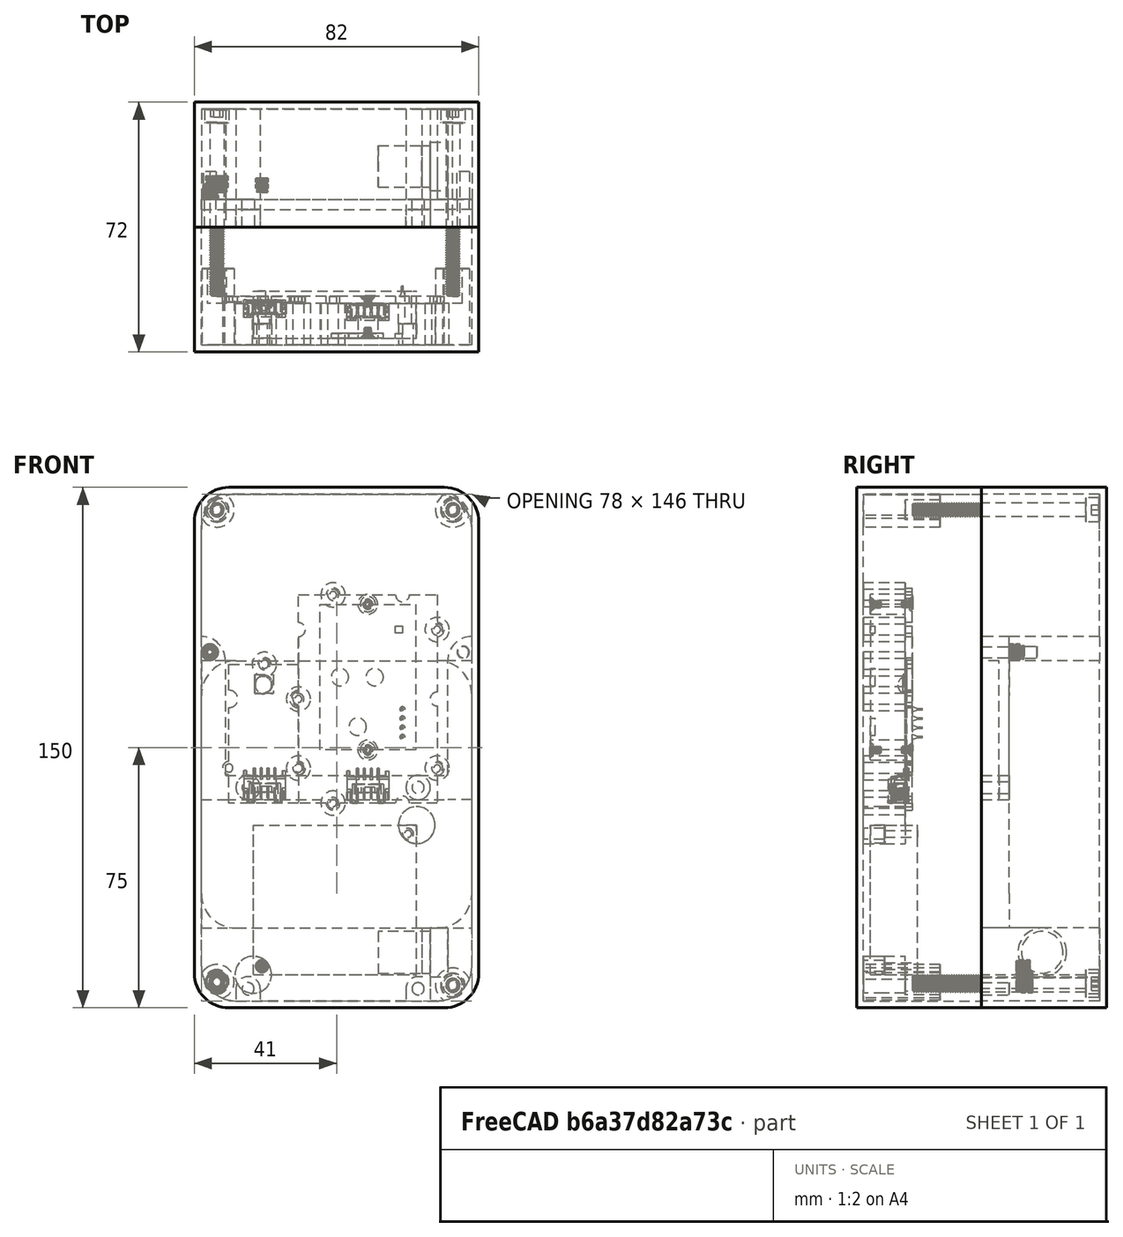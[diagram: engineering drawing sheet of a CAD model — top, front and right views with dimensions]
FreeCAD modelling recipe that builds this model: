
FCSTD DOCUMENT  (FreeCAD 0.20R29177 +233 (Git))
Label: wearableCad_10_10_2022
License: All rights reserved
LicenseURL: http://en.wikipedia.org/wiki/All_rights_reserved
objects: Part::Cylinder×78, Part::Cut×42, Part::Box×36, Part::MultiFuse×24, Part::Feature×10
note: 190 computed .brp shape members not serialized (recipe doc carries the construction recipe); baked Part::Feature solids carry a one-line shape summary decoded from their .brp

FEATURE [Part::Feature] Feature  label="Odroid-C4"
  Placement = pos=(66,-10,0) rot=(0.57735,-0.57735,0.57735;2.0944rad)
  shape: bbox 57.1 x 20.65 x 89.5 mm, 2775 faces, 0 solids (baked)
FEATURE [Part::Feature] Feature001  label="SCD30"
  Placement = pos=(-1.3e-14,-22,57) rot=(0,-1,0;1.5708rad)
  shape: bbox 44 x 15.1 x 64 mm, 422 faces, 13 solids (baked)
FEATURE [Part::Feature] Feature002  label="bme280"
  Placement = pos=(-60,-20,58) rot=(0.707107,0,0.707107;3.14159rad)
  shape: bbox 23.8 x 6.016 x 41.9 mm, 221 faces, 2 solids (baked)
FEATURE [Part::MultiFuse] Fusion  label="i2cSensors"
  Placement = pos=(68,-10,0) rot=(0,0,1;0rad)
  Shapes = -> [Feature001,Feature002]
FEATURE [Part::Box] Box  label="ips7100"
  AttacherType = Attacher::AttachEngine3D
  Height = 43.1
  Length = 47.1
  Width = 13.55
FEATURE [Part::Cylinder] Cylinder
  Angle = 360
  AttacherType = Attacher::AttachEngine3D
  FirstAngle = 0
  Height = 13.55
  Placement = pos=(2.5,13.55,2.5) rot=(1,0,0;1.5708rad)
  Radius = 1
  SecondAngle = 0
FEATURE [Part::Cylinder] Cylinder001  label="semiCut"
  Angle = 90
  AttacherType = Attacher::AttachEngine3D
  FirstAngle = 0
  Height = 4.13
  Placement = pos=(0,4.13,-9e-16) rot=(1,0,0;1.5708rad)
  Radius = 5.25
  SecondAngle = 0
FEATURE [Part::MultiFuse] Fusion001  label="ipsCut"
  Shapes = -> [Cylinder,Cylinder001]
FEATURE [Part::Cylinder] Cylinder002
  Angle = 360
  AttacherType = Attacher::AttachEngine3D
  FirstAngle = 0
  Height = 13.55
  Placement = pos=(2.5,13.55,2.5) rot=(1,0,0;1.5708rad)
  Radius = 1
  SecondAngle = 0
FEATURE [Part::Cylinder] Cylinder003  label="semiCut001"
  Angle = 90
  AttacherType = Attacher::AttachEngine3D
  FirstAngle = 0
  Height = 4.13
  Placement = pos=(0,4.13,-9e-16) rot=(1,0,0;1.5708rad)
  Radius = 5.25
  SecondAngle = 0
FEATURE [Part::MultiFuse] Fusion002  label="ipsCut001"
  Placement = pos=(47.1,0,43.1) rot=(0,1,0;3.14159rad)
  Shapes = -> [Cylinder002,Cylinder003]
FEATURE [Part::MultiFuse] Fusion003
  Shapes = -> [Fusion001,Fusion002]
FEATURE [Part::Cut] Cut  label="ips7100V"
  Base = -> Box
  Placement = pos=(15,-42,7.55) rot=(0,0,1;0rad)
  Tool = -> Fusion003
FEATURE [Part::Box] Box001  label="V25B"
  AttacherType = Attacher::AttachEngine3D
  Height = 77
  Length = 78
  Width = 26
FEATURE [Part::Cylinder] Cylinder004
  Angle = 90
  AttacherType = Attacher::AttachEngine3D
  FirstAngle = 0
  Height = 26
  Placement = pos=(0,26,-5.8e-15) rot=(1,0,0;1.5708rad)
  Radius = 10
  SecondAngle = 0
FEATURE [Part::Box] Box002  label="Cube"
  AttacherType = Attacher::AttachEngine3D
  Height = 10
  Length = 10
  Width = 26
FEATURE [Part::Cut] Cut001
  Base = -> Box002
  Placement = pos=(68,0,67) rot=(0,0,1;0rad)
  Tool = -> Cylinder004
FEATURE [Part::Box] Box003  label="Cube001"
  AttacherType = Attacher::AttachEngine3D
  Height = 10
  Length = 10
  Width = 26
FEATURE [Part::Cylinder] Cylinder005
  Angle = 90
  AttacherType = Attacher::AttachEngine3D
  FirstAngle = 0
  Height = 26
  Placement = pos=(0,26,-5.8e-15) rot=(1,0,0;1.5708rad)
  Radius = 10
  SecondAngle = 0
FEATURE [Part::Cut] Cut002
  Base = -> Box003
  Placement = pos=(68,0,10) rot=(0,1,0;1.5708rad)
  Tool = -> Cylinder005
FEATURE [Part::Box] Box004  label="Cube002"
  AttacherType = Attacher::AttachEngine3D
  Height = 10
  Length = 10
  Width = 26
FEATURE [Part::Cylinder] Cylinder006
  Angle = 90
  AttacherType = Attacher::AttachEngine3D
  FirstAngle = 0
  Height = 26
  Placement = pos=(0,26,-5.8e-15) rot=(1,0,0;1.5708rad)
  Radius = 10
  SecondAngle = 0
FEATURE [Part::Cut] Cut003
  Base = -> Box004
  Placement = pos=(10,0,10) rot=(0,1,0;3.14159rad)
  Tool = -> Cylinder006
FEATURE [Part::Box] Box005  label="Cube003"
  AttacherType = Attacher::AttachEngine3D
  Height = 10
  Length = 10
  Width = 26
FEATURE [Part::Cylinder] Cylinder007
  Angle = 90
  AttacherType = Attacher::AttachEngine3D
  FirstAngle = 0
  Height = 26
  Placement = pos=(0,26,-5.8e-15) rot=(1,0,0;1.5708rad)
  Radius = 10
  SecondAngle = 0
FEATURE [Part::Cut] Cut004
  Base = -> Box005
  Placement = pos=(10,0,67) rot=(0,-1,0;1.5708rad)
  Tool = -> Cylinder007
FEATURE [Part::MultiFuse] Fusion004  label="v25Cuts"
  Shapes = -> [Cut001,Cut002,Cut003,Cut004]
FEATURE [Part::Cut] Cut005  label="V25B001"
  Base = -> Box001
  Placement = pos=(0,-2,21) rot=(0,0,1;0rad)
  Tool = -> Fusion004
FEATURE [Part::Box] Box007  label="Cube004"
  AttacherType = Attacher::AttachEngine3D
  Height = 10
  Length = 10
  Placement = pos=(0,-10,0) rot=(0,0,1;0rad)
  Width = 36
FEATURE [Part::Cylinder] Cylinder008
  Angle = 90
  AttacherType = Attacher::AttachEngine3D
  FirstAngle = 0
  Height = 36
  Placement = pos=(0,26,-5.8e-15) rot=(1,0,0;1.5708rad)
  Radius = 10
  SecondAngle = 0
FEATURE [Part::Cut] Cut006
  Base = -> Box007
  Placement = pos=(8,18,8) rot=(-0.707107,0,0.707107;3.14159rad)
  Tool = -> Cylinder008
FEATURE [Part::Box] Box008  label="baseOut001"
  AttacherType = Attacher::AttachEngine3D
  Height = 150
  Length = 82
  Placement = pos=(80,26,-2) rot=(0,0,1;3.14159rad)
  Width = 36
FEATURE [Part::Box] Box009  label="Cube005"
  AttacherType = Attacher::AttachEngine3D
  Height = 10
  Length = 10
  Placement = pos=(0,-10,0) rot=(0,0,1;0rad)
  Width = 36
FEATURE [Part::Cylinder] Cylinder009
  Angle = 90
  AttacherType = Attacher::AttachEngine3D
  FirstAngle = 0
  Height = 36
  Placement = pos=(0,26,-5.8e-15) rot=(1,0,0;1.5708rad)
  Radius = 10
  SecondAngle = 0
FEATURE [Part::Cut] Cut007
  Base = -> Box009
  Placement = pos=(70,18,8) rot=(1,0,0;3.14159rad)
  Tool = -> Cylinder009
FEATURE [Part::Box] Box010  label="Cube006"
  AttacherType = Attacher::AttachEngine3D
  Height = 10
  Length = 10
  Placement = pos=(0,-10,0) rot=(0,0,1;0rad)
  Width = 36
FEATURE [Part::Cylinder] Cylinder010
  Angle = 90
  AttacherType = Attacher::AttachEngine3D
  FirstAngle = 0
  Height = 36
  Placement = pos=(0,26,-5.8e-15) rot=(1,0,0;1.5708rad)
  Radius = 10
  SecondAngle = 0
FEATURE [Part::Cut] Cut008
  Base = -> Box010
  Placement = pos=(8,18,138) rot=(0,0,1;3.14159rad)
  Tool = -> Cylinder010
FEATURE [Part::Box] Box011  label="Cube007"
  AttacherType = Attacher::AttachEngine3D
  Height = 10
  Length = 10
  Placement = pos=(0,-10,0) rot=(0,0,1;0rad)
  Width = 36
FEATURE [Part::Cylinder] Cylinder011
  Angle = 90
  AttacherType = Attacher::AttachEngine3D
  FirstAngle = 0
  Height = 36
  Placement = pos=(0,26,-5.8e-15) rot=(1,0,0;1.5708rad)
  Radius = 10
  SecondAngle = 0
FEATURE [Part::Cut] Cut009
  Base = -> Box011
  Placement = pos=(70,18,138) rot=(0.707107,0,0.707107;3.14159rad)
  Tool = -> Cylinder011
FEATURE [Part::MultiFuse] Fusion005
  Placement = pos=(0,-2,0) rot=(0,0,1;0rad)
  Shapes = -> [Cut006,Cut007,Cut008,Cut009]
FEATURE [Part::Cut] Cut010  label="BaseOut"
  Base = -> Box008
  Tool = -> Fusion005
FEATURE [Part::Box] Box013  label="Cube009"
  AttacherType = Attacher::AttachEngine3D
  Height = 10
  Length = 10
  Placement = pos=(0,-8,0) rot=(0,0,1;0rad)
  Width = 34
FEATURE [Part::Box] Box014  label="baseOut002"
  AttacherType = Attacher::AttachEngine3D
  Height = 146
  Length = 78
  Placement = pos=(80,26,-2) rot=(0,0,1;3.14159rad)
  Width = 34
FEATURE [Part::Box] Box015  label="Cube010"
  AttacherType = Attacher::AttachEngine3D
  Height = 10
  Length = 10
  Placement = pos=(0,-8,0) rot=(0,0,1;0rad)
  Width = 34
FEATURE [Part::Box] Box016  label="Cube011"
  AttacherType = Attacher::AttachEngine3D
  Height = 10
  Length = 10
  Placement = pos=(0,-8,0) rot=(0,0,1;0rad)
  Width = 34
FEATURE [Part::Box] Box017  label="Cube012"
  AttacherType = Attacher::AttachEngine3D
  Height = 10
  Length = 10
  Placement = pos=(0,-8,0) rot=(0,0,1;0rad)
  Width = 34
FEATURE [Part::Cylinder] Cylinder013
  Angle = 90
  AttacherType = Attacher::AttachEngine3D
  FirstAngle = 0
  Height = 34
  Placement = pos=(0,26,-5.8e-15) rot=(1,0,0;1.5708rad)
  Radius = 10
  SecondAngle = 0
FEATURE [Part::Cut] Cut012
  Base = -> Box013
  Placement = pos=(12,18,8) rot=(0.707107,0,-0.707107;3.14159rad)
  Tool = -> Cylinder013
FEATURE [Part::Cylinder] Cylinder014
  Angle = 90
  AttacherType = Attacher::AttachEngine3D
  FirstAngle = 0
  Height = 34
  Placement = pos=(0,26,-5.8e-15) rot=(1,0,0;1.5708rad)
  Radius = 10
  SecondAngle = 0
FEATURE [Part::Cut] Cut013
  Base = -> Box015
  Placement = pos=(70,18,8) rot=(1,0,0;3.14159rad)
  Tool = -> Cylinder014
FEATURE [Part::Cylinder] Cylinder015
  Angle = 90
  AttacherType = Attacher::AttachEngine3D
  FirstAngle = 0
  Height = 34
  Placement = pos=(0,26,-5.8e-15) rot=(1,0,0;1.5708rad)
  Radius = 10
  SecondAngle = 0
FEATURE [Part::Cut] Cut014
  Base = -> Box016
  Placement = pos=(12,18,134) rot=(0,0,1;3.14159rad)
  Tool = -> Cylinder015
FEATURE [Part::Cylinder] Cylinder016
  Angle = 90
  AttacherType = Attacher::AttachEngine3D
  FirstAngle = 0
  Height = 34
  Placement = pos=(0,26,-5.8e-15) rot=(1,0,0;1.5708rad)
  Radius = 10
  SecondAngle = 0
FEATURE [Part::Cut] Cut015
  Base = -> Box017
  Placement = pos=(70,18,135) rot=(0.707107,0,0.707107;3.14159rad)
  Tool = -> Cylinder016
FEATURE [Part::MultiFuse] Fusion006
  Shapes = -> [Cut012,Cut013,Cut014,Cut015]
FEATURE [Part::Cut] Cut016  label="BaseOut001"
  Base = -> Box014
  Placement = pos=(-2,-2,2) rot=(0,0,1;0rad)
  Tool = -> Fusion006
FEATURE [Part::Cut] Cut017  label="baseOut"
  Base = -> Cut010
  Tool = -> Cut016
FEATURE [Part::Box] Box018  label="Cube013"
  AttacherType = Attacher::AttachEngine3D
  Height = 10
  Length = 10
  Placement = pos=(10,26,0) rot=(0,0,-1;3.14159rad)
  Width = 26
FEATURE [Part::Cylinder] Cylinder017
  Angle = 90
  AttacherType = Attacher::AttachEngine3D
  FirstAngle = 0
  Height = 26
  Placement = pos=(0,26,-5.8e-15) rot=(1,0,0;1.5708rad)
  Radius = 10
  SecondAngle = 0
FEATURE [Part::Cut] Cut018  label="batterySupport"
  Base = -> Box018
  Placement = pos=(10,-2,31) rot=(0,1,0;3.14159rad)
  Tool = -> Cylinder017
FEATURE [Part::Box] Box019  label="Cube014"
  AttacherType = Attacher::AttachEngine3D
  Height = 10
  Length = 10
  Placement = pos=(10,26,0) rot=(0,0,1;3.14159rad)
  Width = 26
FEATURE [Part::Cylinder] Cylinder018
  Angle = 90
  AttacherType = Attacher::AttachEngine3D
  FirstAngle = 0
  Height = 26
  Placement = pos=(0,26,-5.8e-15) rot=(1,0,0;1.5708rad)
  Radius = 10
  SecondAngle = 0
FEATURE [Part::Cut] Cut019  label="batterySupport001"
  Base = -> Box019
  Placement = pos=(68,-2,31) rot=(0,-1,0;4.71239rad)
  Tool = -> Cylinder018
FEATURE [Part::Box] Box020  label="Cube015"
  AttacherType = Attacher::AttachEngine3D
  Height = 10
  Length = 10
  Placement = pos=(10,26,0) rot=(0,0,1;3.14159rad)
  Width = 26
FEATURE [Part::Cylinder] Cylinder019
  Angle = 90
  AttacherType = Attacher::AttachEngine3D
  FirstAngle = 0
  Height = 26
  Placement = pos=(0,26,-5.8e-15) rot=(1,0,0;1.5708rad)
  Radius = 10
  SecondAngle = 0
FEATURE [Part::Cut] Cut020  label="batterySupport002"
  Base = -> Box020
  Placement = pos=(68,-2,88) rot=(0,0,1;0rad)
  Tool = -> Cylinder019
FEATURE [Part::Box] Box021  label="Cube016"
  AttacherType = Attacher::AttachEngine3D
  Height = 10
  Length = 10
  Placement = pos=(10,26,0) rot=(0,0,1;3.14159rad)
  Width = 26
FEATURE [Part::Cylinder] Cylinder020
  Angle = 90
  AttacherType = Attacher::AttachEngine3D
  FirstAngle = 0
  Height = 26
  Placement = pos=(0,26,-5.8e-15) rot=(1,0,0;1.5708rad)
  Radius = 10
  SecondAngle = 0
FEATURE [Part::Cut] Cut021  label="batterySupport003"
  Base = -> Box021
  Placement = pos=(10,-2,88) rot=(0,1,0;4.71239rad)
  Tool = -> Cylinder020
FEATURE [Part::Cylinder] Cylinder021
  Angle = 360
  AttacherType = Attacher::AttachEngine3D
  FirstAngle = 0
  Height = 34
  Placement = pos=(13.5,24,3.5) rot=(1,0,0;1.5708rad)
  Radius = 3.5
  SecondAngle = 0
FEATURE [Part::Cylinder] Cylinder022
  Angle = 360
  AttacherType = Attacher::AttachEngine3D
  FirstAngle = 0
  Height = 8
  Placement = pos=(13.5,-2,3.5) rot=(1,0,0;1.5708rad)
  Radius = 1.75
  SecondAngle = 0
FEATURE [Part::Box] Box022  label="Cube017"
  AttacherType = Attacher::AttachEngine3D
  Height = 3.5
  Length = 7
  Placement = pos=(10,24,3.5) rot=(1,0,0;3.14159rad)
  Width = 34
FEATURE [Part::Cylinder] Cylinder023
  Angle = 360
  AttacherType = Attacher::AttachEngine3D
  FirstAngle = 0
  Height = 34
  Placement = pos=(62.5,24,3.5) rot=(1,0,0;1.5708rad)
  Radius = 3.5
  SecondAngle = 0
FEATURE [Part::Cylinder] Cylinder024
  Angle = 360
  AttacherType = Attacher::AttachEngine3D
  FirstAngle = 0
  Height = 8
  Placement = pos=(62.5,-2,3.5) rot=(1,0,0;1.5708rad)
  Radius = 1.75
  SecondAngle = 0
FEATURE [Part::Box] Box023  label="Cube018"
  AttacherType = Attacher::AttachEngine3D
  Height = 3.5
  Length = 7
  Placement = pos=(59,24,3.5) rot=(1,0,0;3.14159rad)
  Width = 34
FEATURE [Part::Cylinder] Cylinder025
  Angle = 360
  AttacherType = Attacher::AttachEngine3D
  FirstAngle = 0
  Height = 20
  Radius = 6
  SecondAngle = 0
FEATURE [Part::Cylinder] Cylinder026
  Angle = 360
  AttacherType = Attacher::AttachEngine3D
  FirstAngle = 0
  Height = 5
  Radius = 7
  SecondAngle = 0
FEATURE [Part::MultiFuse] Fusion007  label="powerSwitch"
  Placement = pos=(71,7.5,14) rot=(0,1,0;4.71239rad)
  Shapes = -> [Cylinder025,Cylinder026]
FEATURE [Part::Box] Box024  label="Cube019"
  AttacherType = Attacher::AttachEngine3D
  Height = 17.5
  Length = 2.5
  Placement = pos=(63.5,24,21) rot=(1,0,0;3.14159rad)
  Width = 34
FEATURE [Part::MultiFuse] Fusion008  label="base"
  Shapes = -> [Cut017,Cut018,Cut019,Cut020,Cut021]
FEATURE [Part::MultiFuse] Fusion009  label="base001"
  Shapes = -> [Cylinder021,Cylinder023,Box022,Box023,Box024,Fusion008]
FEATURE [Part::MultiFuse] Fusion010  label="baseCuts"
  Shapes = -> [Cylinder024,Cylinder022,Fusion007]
FEATURE [Part::Cut] Cut022  label="base002"
  Base = -> Fusion009
  Tool = -> Fusion010
FEATURE [Part::Cylinder] Cylinder027  label="mainMounts"
  Angle = 90
  AttacherType = Attacher::AttachEngine3D
  FirstAngle = 0
  Height = 26
  Placement = pos=(0,24,98) rot=(1,0,0;1.5708rad)
  Radius = 7
  SecondAngle = 0
FEATURE [Part::Cylinder] Cylinder028  label="mainMounts001"
  Angle = 90
  AttacherType = Attacher::AttachEngine3D
  FirstAngle = 0
  Height = 26
  Placement = pos=(78,24,98) rot=(0.57735,-0.57735,0.57735;2.0944rad)
  Radius = 7
  SecondAngle = 0
FEATURE [Part::Cylinder] Cylinder029
  Angle = 360
  AttacherType = Attacher::AttachEngine3D
  FirstAngle = 0
  Height = 8
  Placement = pos=(2.5,-2,100.5) rot=(1,0,0;1.5708rad)
  Radius = 1.75
  SecondAngle = 0
FEATURE [Part::Cylinder] Cylinder030
  Angle = 360
  AttacherType = Attacher::AttachEngine3D
  FirstAngle = 0
  Height = 8
  Placement = pos=(75.5,-2,100.5) rot=(1,0,0;1.5708rad)
  Radius = 1.75
  SecondAngle = 0
FEATURE [Part::MultiFuse] Fusion011  label="baseCuts001"
  Placement = pos=(0,8,0) rot=(0,0,1;0rad)
  Shapes = -> [Cylinder029,Cylinder030]
FEATURE [Part::MultiFuse] Fusion012
  Shapes = -> [Cylinder028,Cylinder027]
FEATURE [Part::MultiFuse] Fusion013  label="base003"
  Shapes = -> [Cut022,Fusion012]
FEATURE [Part::Cut] Cut023  label="baseBottom"
  Base = -> Fusion013
  Tool = -> Fusion011
FEATURE [Part::Feature] Solid  label="m3HeatSet"
  Placement = pos=(2.5,2.3,100.5) rot=(1,0,0;3.14159rad)
  shape: bbox 4.772 x 4.354 x 4.772 mm, 239 faces (baked)
FEATURE [Part::Cylinder] Cylinder031
  Angle = 360
  AttacherType = Attacher::AttachEngine3D
  FirstAngle = 0
  Height = 8
  Placement = pos=(13.5,-2,61.5) rot=(1,0,0;1.5708rad)
  Radius = 3.5
  SecondAngle = 0
FEATURE [Part::Cylinder] Cylinder032  label="cuts"
  Angle = 360
  AttacherType = Attacher::AttachEngine3D
  FirstAngle = 0
  Height = 8
  Placement = pos=(13.5,-2,61.5) rot=(1,0,0;1.5708rad)
  Radius = 1.75
  SecondAngle = 0
FEATURE [Part::Cylinder] Cylinder034
  Angle = 360
  AttacherType = Attacher::AttachEngine3D
  FirstAngle = 0
  Height = 8
  Placement = pos=(62.5,-2,61.5) rot=(1,0,0;1.5708rad)
  Radius = 3.5
  SecondAngle = 0
FEATURE [Part::Cylinder] Cylinder035  label="cuts001"
  Angle = 360
  AttacherType = Attacher::AttachEngine3D
  FirstAngle = 0
  Height = 8
  Placement = pos=(62.5,-2,61.5) rot=(1,0,0;1.5708rad)
  Radius = 1.75
  SecondAngle = 0
FEATURE [Part::Cylinder] Cylinder036
  Angle = 90
  AttacherType = Attacher::AttachEngine3D
  FirstAngle = 0
  Height = 8
  Placement = pos=(78,-2,98) rot=(-0.57735,0.57735,-0.57735;4.18879rad)
  Radius = 7
  SecondAngle = 0
FEATURE [Part::Cylinder] Cylinder037
  Angle = 90
  AttacherType = Attacher::AttachEngine3D
  FirstAngle = 0
  Height = 8
  Placement = pos=(0,-2,98) rot=(1,0,0;1.5708rad)
  Radius = 7
  SecondAngle = 0
FEATURE [Part::Box] Box025  label="Cube020"
  AttacherType = Attacher::AttachEngine3D
  Height = 7
  Length = 78
  Placement = pos=(0,-5,58) rot=(0,0,1;0rad)
  Width = 3
FEATURE [Part::Box] Box026  label="Cube021"
  AttacherType = Attacher::AttachEngine3D
  Height = 7
  Length = 40
  Placement = pos=(7,-5,58) rot=(0,1,0;4.71239rad)
  Width = 3
FEATURE [Part::Box] Box027  label="Cube022"
  AttacherType = Attacher::AttachEngine3D
  Height = 7
  Length = 40
  Placement = pos=(78,-5,58) rot=(0,-1,0;1.5708rad)
  Width = 3
FEATURE [Part::MultiFuse] Fusion014
  Shapes = -> [Box027,Box025,Box026,Cylinder034,Cylinder031]
FEATURE [Part::Cylinder] Cylinder038  label="m3Screw"
  Angle = 360
  AttacherType = Attacher::AttachEngine3D
  FirstAngle = 0
  Height = 8
  Placement = pos=(75.5,-2,100.5) rot=(1,0,0;1.5708rad)
  Radius = 1.6
  SecondAngle = 0
FEATURE [Part::Cylinder] Cylinder039  label="m3Screw001"
  Angle = 360
  AttacherType = Attacher::AttachEngine3D
  FirstAngle = 0
  Height = 8
  Placement = pos=(2.5,-2,100.5) rot=(1,0,0;1.5708rad)
  Radius = 1.6
  SecondAngle = 0
FEATURE [Part::MultiFuse] Fusion015  label="c4Hold"
  Shapes = -> [Cylinder036,Cylinder037,Fusion014]
FEATURE [Part::MultiFuse] Fusion016  label="c4oldCuts"
  Shapes = -> [Cylinder039,Cylinder032,Cylinder035,Cylinder038]
FEATURE [Part::Cut] Cut024  label="c4Hold001"
  Base = -> Fusion015
  Tool = -> Fusion016
FEATURE [Part::Box] Box028  label="Cube023"
  AttacherType = Attacher::AttachEngine3D
  Height = 10
  Length = 10
  Placement = pos=(0,-10,0) rot=(0,0,1;0rad)
  Width = 36
FEATURE [Part::Box] Box029  label="baseOut003"
  AttacherType = Attacher::AttachEngine3D
  Height = 150
  Length = 82
  Placement = pos=(80,26,-2) rot=(0,0,1;3.14159rad)
  Width = 36
FEATURE [Part::Box] Box030  label="Cube024"
  AttacherType = Attacher::AttachEngine3D
  Height = 10
  Length = 10
  Placement = pos=(0,-10,0) rot=(0,0,1;0rad)
  Width = 36
FEATURE [Part::Box] Box031  label="Cube025"
  AttacherType = Attacher::AttachEngine3D
  Height = 10
  Length = 10
  Placement = pos=(0,-10,0) rot=(0,0,1;0rad)
  Width = 36
FEATURE [Part::Box] Box032  label="Cube026"
  AttacherType = Attacher::AttachEngine3D
  Height = 10
  Length = 10
  Placement = pos=(0,-10,0) rot=(0,0,1;0rad)
  Width = 36
FEATURE [Part::Box] Box033  label="Cube027"
  AttacherType = Attacher::AttachEngine3D
  Height = 10
  Length = 10
  Placement = pos=(0,-8,0) rot=(0,0,1;0rad)
  Width = 34
FEATURE [Part::Box] Box034  label="baseOut004"
  AttacherType = Attacher::AttachEngine3D
  Height = 146
  Length = 78
  Placement = pos=(80,26,-2) rot=(0,0,1;3.14159rad)
  Width = 34
FEATURE [Part::Box] Box035  label="Cube028"
  AttacherType = Attacher::AttachEngine3D
  Height = 10
  Length = 10
  Placement = pos=(0,-8,0) rot=(0,0,1;0rad)
  Width = 34
FEATURE [Part::Box] Box036  label="Cube029"
  AttacherType = Attacher::AttachEngine3D
  Height = 10
  Length = 10
  Placement = pos=(0,-8,0) rot=(0,0,1;0rad)
  Width = 34
FEATURE [Part::Box] Box037  label="Cube030"
  AttacherType = Attacher::AttachEngine3D
  Height = 10
  Length = 10
  Placement = pos=(0,-8,0) rot=(0,0,1;0rad)
  Width = 34
FEATURE [Part::Cylinder] Cylinder040
  Angle = 90
  AttacherType = Attacher::AttachEngine3D
  FirstAngle = 0
  Height = 36
  Placement = pos=(0,26,-5.8e-15) rot=(1,0,0;1.5708rad)
  Radius = 10
  SecondAngle = 0
FEATURE [Part::Cut] Cut025
  Base = -> Box028
  Placement = pos=(8,18,8) rot=(0.707107,0,-0.707107;3.14159rad)
  Tool = -> Cylinder040
FEATURE [Part::Cylinder] Cylinder041
  Angle = 90
  AttacherType = Attacher::AttachEngine3D
  FirstAngle = 0
  Height = 36
  Placement = pos=(0,26,-5.8e-15) rot=(1,0,0;1.5708rad)
  Radius = 10
  SecondAngle = 0
FEATURE [Part::Cut] Cut026
  Base = -> Box030
  Placement = pos=(70,18,8) rot=(1,0,0;3.14159rad)
  Tool = -> Cylinder041
FEATURE [Part::Cylinder] Cylinder042
  Angle = 90
  AttacherType = Attacher::AttachEngine3D
  FirstAngle = 0
  Height = 36
  Placement = pos=(0,26,-5.8e-15) rot=(1,0,0;1.5708rad)
  Radius = 10
  SecondAngle = 0
FEATURE [Part::Cut] Cut027
  Base = -> Box031
  Placement = pos=(8,18,138) rot=(0,0,1;3.14159rad)
  Tool = -> Cylinder042
FEATURE [Part::Cylinder] Cylinder043
  Angle = 90
  AttacherType = Attacher::AttachEngine3D
  FirstAngle = 0
  Height = 36
  Placement = pos=(0,26,-5.8e-15) rot=(1,0,0;1.5708rad)
  Radius = 10
  SecondAngle = 0
FEATURE [Part::Cut] Cut028
  Base = -> Box032
  Placement = pos=(70,18,138) rot=(0.707107,0,0.707107;3.14159rad)
  Tool = -> Cylinder043
FEATURE [Part::Cylinder] Cylinder044
  Angle = 90
  AttacherType = Attacher::AttachEngine3D
  FirstAngle = 0
  Height = 34
  Placement = pos=(0,26,-5.8e-15) rot=(1,0,0;1.5708rad)
  Radius = 10
  SecondAngle = 0
FEATURE [Part::Cut] Cut030
  Base = -> Box033
  Placement = pos=(12,18,8) rot=(0.707107,0,-0.707107;3.14159rad)
  Tool = -> Cylinder044
FEATURE [Part::Cylinder] Cylinder045
  Angle = 90
  AttacherType = Attacher::AttachEngine3D
  FirstAngle = 0
  Height = 34
  Placement = pos=(0,26,-5.8e-15) rot=(1,0,0;1.5708rad)
  Radius = 10
  SecondAngle = 0
FEATURE [Part::Cut] Cut031
  Base = -> Box035
  Placement = pos=(70,18,8) rot=(1,0,0;3.14159rad)
  Tool = -> Cylinder045
FEATURE [Part::Cylinder] Cylinder046
  Angle = 90
  AttacherType = Attacher::AttachEngine3D
  FirstAngle = 0
  Height = 34
  Placement = pos=(0,26,-5.8e-15) rot=(1,0,0;1.5708rad)
  Radius = 10
  SecondAngle = 0
FEATURE [Part::Cut] Cut032
  Base = -> Box036
  Placement = pos=(12,18,134) rot=(0,0,1;3.14159rad)
  Tool = -> Cylinder046
FEATURE [Part::Cylinder] Cylinder047
  Angle = 90
  AttacherType = Attacher::AttachEngine3D
  FirstAngle = 0
  Height = 34
  Placement = pos=(0,26,-5.8e-15) rot=(1,0,0;1.5708rad)
  Radius = 10
  SecondAngle = 0
FEATURE [Part::Cut] Cut033
  Base = -> Box037
  Placement = pos=(70,18,135) rot=(0.707107,0,0.707107;3.14159rad)
  Tool = -> Cylinder047
FEATURE [Part::MultiFuse] Fusion017
  Placement = pos=(0,-2,0) rot=(0,0,1;0rad)
  Shapes = -> [Cut025,Cut026,Cut027,Cut028]
FEATURE [Part::Cut] Cut029  label="BaseOut002"
  Base = -> Box029
  Tool = -> Fusion017
FEATURE [Part::MultiFuse] Fusion018
  Shapes = -> [Cut030,Cut031,Cut032,Cut033]
FEATURE [Part::Cut] Cut034  label="BaseOut003"
  Base = -> Box034
  Placement = pos=(-2,-2,2) rot=(0,0,1;0rad)
  Tool = -> Fusion018
FEATURE [Part::Cut] Cut035  label="baseTop"
  Base = -> Cut029
  Placement = pos=(78,-20,0) rot=(0,0,1;3.14159rad)
  Tool = -> Cut034
FEATURE [Part::Feature] Solid001  label="m2HeatSet"
  Placement = pos=(17.5,0,10) rot=(0,0,1;0rad)
  shape: bbox 3.655 x 4.083 x 3.655 mm, 239 faces (baked)
FEATURE [Part::Cylinder] Cylinder048
  Angle = 360
  AttacherType = Attacher::AttachEngine3D
  FirstAngle = 0
  Height = 6
  Placement = pos=(17.5,-44,10.05) rot=(1,0,0;4.71239rad)
  Radius = 1.57
  SecondAngle = 0
FEATURE [Part::Cylinder] Cylinder049
  Angle = 360
  AttacherType = Attacher::AttachEngine3D
  FirstAngle = 0
  Height = 6
  Placement = pos=(15,-44,7.55) rot=(0.57735,0.57735,0.57735;4.18879rad)
  Radius = 5.3
  SecondAngle = 0
FEATURE [Part::Cylinder] Cylinder050
  Angle = 360
  AttacherType = Attacher::AttachEngine3D
  FirstAngle = 0
  Height = 6
  Placement = pos=(62.1,-44,50.65) rot=(0.57735,-0.57735,-0.57735;4.18879rad)
  Radius = 5.3
  SecondAngle = 0
FEATURE [Part::Cylinder] Cylinder051
  Angle = 360
  AttacherType = Attacher::AttachEngine3D
  FirstAngle = 0
  Height = 6
  Placement = pos=(59.6,-44,48.15) rot=(-1,0,0;1.5708rad)
  Radius = 1.57
  SecondAngle = 0
FEATURE [Part::Cut] Cut036
  Base = -> Cylinder049
  Tool = -> Cylinder048
FEATURE [Part::Cut] Cut037
  Base = -> Cylinder050
  Tool = -> Cylinder051
FEATURE [Part::Cylinder] Cylinder052
  Angle = 270
  AttacherType = Attacher::AttachEngine3D
  FirstAngle = 0
  Height = 6
  Placement = pos=(15,-38,7.55) rot=(-1,0,0;1.5708rad)
  Radius = 5.3
  SecondAngle = 0
FEATURE [Part::Cylinder] Cylinder053
  Angle = 270
  AttacherType = Attacher::AttachEngine3D
  FirstAngle = 0
  Height = 6
  Placement = pos=(62.1,-38,50.65) rot=(0,-0.707107,-0.707107;3.14159rad)
  Radius = 5.3
  SecondAngle = 0
FEATURE [Part::MultiFuse] Fusion019  label="baseTop001"
  Shapes = -> [Cut036,Cut037,Cylinder052,Cylinder053,Cut035]
FEATURE [Part::Cylinder] Cylinder054  label="m2HeatSet001"
  Angle = 360
  AttacherType = Attacher::AttachEngine3D
  FirstAngle = 0
  Height = 12
  Placement = pos=(8,-44,67.1) rot=(-1,0,0;1.5708rad)
  Radius = 1.6
  SecondAngle = 0
FEATURE [Part::Cylinder] Cylinder055  label="m2HeatSet002"
  Angle = 360
  AttacherType = Attacher::AttachEngine3D
  FirstAngle = 0
  Height = 12
  Placement = pos=(28,-44,67.1) rot=(-1,0,0;1.5708rad)
  Radius = 1.6
  SecondAngle = 0
FEATURE [Part::Cylinder] Cylinder056  label="m2HeatSet003"
  Angle = 360
  AttacherType = Attacher::AttachEngine3D
  FirstAngle = 0
  Height = 12
  Placement = pos=(68,-44,67.1) rot=(-1,0,0;1.5708rad)
  Radius = 1.6
  SecondAngle = 0
FEATURE [Part::Cylinder] Cylinder057  label="m2HeatSet004"
  Angle = 360
  AttacherType = Attacher::AttachEngine3D
  FirstAngle = 0
  Height = 12
  Placement = pos=(18.2,-44,97) rot=(-1,0,0;1.5708rad)
  Radius = 1.6
  SecondAngle = 0
FEATURE [Part::Cylinder] Cylinder058  label="m2HeatSet005"
  Angle = 360
  AttacherType = Attacher::AttachEngine3D
  FirstAngle = 0
  Height = 12
  Placement = pos=(28,-44,87) rot=(-1,0,0;1.5708rad)
  Radius = 1.6
  SecondAngle = 0
FEATURE [Part::Cylinder] Cylinder059  label="m2HeatSet006"
  Angle = 360
  AttacherType = Attacher::AttachEngine3D
  FirstAngle = 0
  Height = 12
  Placement = pos=(38,-44,117) rot=(-1,0,0;1.5708rad)
  Radius = 1.6
  SecondAngle = 0
FEATURE [Part::Cylinder] Cylinder060  label="m2HeatSet007"
  Angle = 360
  AttacherType = Attacher::AttachEngine3D
  FirstAngle = 0
  Height = 12
  Placement = pos=(38,-44,57) rot=(-1,0,0;1.5708rad)
  Radius = 1.6
  SecondAngle = 0
FEATURE [Part::Cylinder] Cylinder061  label="m2HeatSet008"
  Angle = 360
  AttacherType = Attacher::AttachEngine3D
  FirstAngle = 0
  Height = 12
  Placement = pos=(68,-44,107) rot=(-1,0,0;1.5708rad)
  Radius = 1.6
  SecondAngle = 0
FEATURE [Part::Cylinder] Cylinder062  label="m2HeatSetOut"
  Angle = 360
  AttacherType = Attacher::AttachEngine3D
  FirstAngle = 0
  Height = 12
  Placement = pos=(8,-44,67.1) rot=(-1,0,0;1.5708rad)
  Radius = 3.5
  SecondAngle = 0
FEATURE [Part::Cylinder] Cylinder063  label="m2HeatSetOut001"
  Angle = 360
  AttacherType = Attacher::AttachEngine3D
  FirstAngle = 0
  Height = 12
  Placement = pos=(28,-44,67.1) rot=(-1,0,0;1.5708rad)
  Radius = 3.5
  SecondAngle = 0
FEATURE [Part::Cylinder] Cylinder064  label="m2HeatSetOut002"
  Angle = 360
  AttacherType = Attacher::AttachEngine3D
  FirstAngle = 0
  Height = 12
  Placement = pos=(18.2,-44,97) rot=(-1,0,0;1.5708rad)
  Radius = 3.5
  SecondAngle = 0
FEATURE [Part::Cylinder] Cylinder065  label="m2HeatSetOut003"
  Angle = 360
  AttacherType = Attacher::AttachEngine3D
  FirstAngle = 0
  Height = 12
  Placement = pos=(68,-44,67.1) rot=(-1,0,0;1.5708rad)
  Radius = 3.5
  SecondAngle = 0
FEATURE [Part::Cylinder] Cylinder066  label="m2HeatSetOut004"
  Angle = 360
  AttacherType = Attacher::AttachEngine3D
  FirstAngle = 0
  Height = 12
  Placement = pos=(28,-44,87) rot=(-1,0,0;1.5708rad)
  Radius = 3.5
  SecondAngle = 0
FEATURE [Part::Cylinder] Cylinder067  label="m2HeatSetOut005"
  Angle = 360
  AttacherType = Attacher::AttachEngine3D
  FirstAngle = 0
  Height = 12
  Placement = pos=(38,-44,57) rot=(-1,0,0;1.5708rad)
  Radius = 3.5
  SecondAngle = 0
FEATURE [Part::Cylinder] Cylinder068  label="m2HeatSetOut006"
  Angle = 360
  AttacherType = Attacher::AttachEngine3D
  FirstAngle = 0
  Height = 12
  Placement = pos=(68,-44,107) rot=(-1,0,0;1.5708rad)
  Radius = 3.5
  SecondAngle = 0
FEATURE [Part::Cylinder] Cylinder069  label="m2HeatSetOut007"
  Angle = 360
  AttacherType = Attacher::AttachEngine3D
  FirstAngle = 0
  Height = 12
  Placement = pos=(38,-44,117) rot=(-1,0,0;1.5708rad)
  Radius = 3.5
  SecondAngle = 0
FEATURE [Part::MultiFuse] Fusion020  label="baseTop002"
  Shapes = -> [Cylinder069,Cylinder063,Cylinder064,Cylinder065,Cylinder066,Cylinder067,Cylinder068,Fusion019]
FEATURE [Part::MultiFuse] Fusion021  label="m2HeatSetCuts"
  Shapes = -> [Cylinder062,Cylinder054,Cylinder055,Cylinder056,Cylinder057,Cylinder058,Cylinder059,Cylinder060,Cylinder061]
FEATURE [Part::Cut] Cut038  label="baseTop003"
  Base = -> Fusion020
  Tool = -> Fusion021
FEATURE [Part::Cylinder] Cylinder070
  Angle = 360
  AttacherType = Attacher::AttachEngine3D
  FirstAngle = 0
  Height = 20
  Radius = 6
  SecondAngle = 0
FEATURE [Part::Cylinder] Cylinder071
  Angle = 360
  AttacherType = Attacher::AttachEngine3D
  FirstAngle = 0
  Height = 5
  Radius = 7
  SecondAngle = 0
FEATURE [Part::MultiFuse] Fusion022  label="powerSwitch001"
  Placement = pos=(71,7.5,14) rot=(0,-1,0;1.5708rad)
  Shapes = -> [Cylinder070,Cylinder071]
FEATURE [Part::Feature] Solid002  label="M4Screw"
  Placement = pos=(72.5,-30,4.5) rot=(-0.57735,0.57735,-0.57735;4.18879rad)
  shape: bbox 7.001 x 54.15 x 7.001 mm, 147 faces (baked)
FEATURE [Part::Feature] Solid003  label="M4Screw001"
  Placement = pos=(4.5,-30,5.5) rot=(0.57735,-0.57735,0.57735;2.0944rad)
  shape: bbox 7.001 x 54.15 x 7.001 mm, 147 faces (baked)
FEATURE [Part::Feature] Solid004  label="M4Screw002"
  Placement = pos=(4.5,-30,141.5) rot=(0.57735,-0.57735,0.57735;2.0944rad)
  shape: bbox 7.001 x 54.15 x 7.001 mm, 147 faces (baked)
FEATURE [Part::Feature] Solid005  label="M4Screw003"
  Placement = pos=(72.5,-30,141.5) rot=(0.57735,-0.57735,0.57735;2.0944rad)
  shape: bbox 7.001 x 54.15 x 7.001 mm, 147 faces (baked)
FEATURE [Part::Cylinder] Cylinder072  label="m4HoleBase"
  Angle = 360
  AttacherType = Attacher::AttachEngine3D
  FirstAngle = 0
  Height = 22
  Placement = pos=(4.5,-44,141.5) rot=(-0.377964,-0.654654,-0.654654;2.41886rad)
  Radius = 4.99
  SecondAngle = 0
FEATURE [Part::Cylinder] Cylinder073  label="m4HeatSetCut"
  Angle = 360
  AttacherType = Attacher::AttachEngine3D
  FirstAngle = 0
  Height = 10
  Placement = pos=(4.5,-32,141.5) rot=(-1,0,0;1.5708rad)
  Radius = 2.8
  SecondAngle = 0
FEATURE [Part::Cut] Cut039  label="m4HeatSetHoles"
  Base = -> Cylinder072
  Tool = -> Cylinder073
FEATURE [Part::Cylinder] Cylinder074  label="m4HoleBase001"
  Angle = 360
  AttacherType = Attacher::AttachEngine3D
  FirstAngle = 0
  Height = 22
  Placement = pos=(4.5,-44,141.5) rot=(0.377964,0.654654,0.654654;3.86433rad)
  Radius = 4.99
  SecondAngle = 0
FEATURE [Part::Cylinder] Cylinder075  label="m4HeatSetCut001"
  Angle = 360
  AttacherType = Attacher::AttachEngine3D
  FirstAngle = 0
  Height = 10
  Placement = pos=(4.5,-32,141.5) rot=(-1,0,0;1.5708rad)
  Radius = 2.8
  SecondAngle = 0
FEATURE [Part::Cut] Cut040  label="m4HeatSetHoles001"
  Base = -> Cylinder074
  Placement = pos=(68,0,0) rot=(0,0,1;0rad)
  Tool = -> Cylinder075
FEATURE [Part::Cylinder] Cylinder076  label="m4HoleBase002"
  Angle = 360
  AttacherType = Attacher::AttachEngine3D
  FirstAngle = 0
  Height = 22
  Placement = pos=(4.5,-44,141.5) rot=(0.377964,0.654654,0.654654;3.86433rad)
  Radius = 4.99
  SecondAngle = 0
FEATURE [Part::Cylinder] Cylinder077  label="m4HeatSetCut002"
  Angle = 360
  AttacherType = Attacher::AttachEngine3D
  FirstAngle = 0
  Height = 10
  Placement = pos=(4.5,-32,141.5) rot=(-1,0,0;1.5708rad)
  Radius = 2.8
  SecondAngle = 0
FEATURE [Part::Cut] Cut041  label="m4HeatSetHoles002"
  Base = -> Cylinder076
  Placement = pos=(0,0,-136) rot=(0,0,1;0rad)
  Tool = -> Cylinder077
FEATURE [Part::Cylinder] Cylinder078  label="m4HoleBase003"
  Angle = 360
  AttacherType = Attacher::AttachEngine3D
  FirstAngle = 0
  Height = 22
  Placement = pos=(4.5,-44,141.5) rot=(0.377964,0.654654,0.654654;3.86433rad)
  Radius = 4.99
  SecondAngle = 0
FEATURE [Part::Cylinder] Cylinder079  label="m4HeatSetCut003"
  Angle = 360
  AttacherType = Attacher::AttachEngine3D
  FirstAngle = 0
  Height = 10
  Placement = pos=(4.5,-32,141.5) rot=(-1,0,0;1.5708rad)
  Radius = 2.8
  SecondAngle = 0
FEATURE [Part::Cut] Cut042  label="m4HeatSetHoles003"
  Base = -> Cylinder078
  Placement = pos=(68,0,-137) rot=(0,0,1;0rad)
  Tool = -> Cylinder079
FEATURE [Part::MultiFuse] Fusion023  label="baseTop004"
  Shapes = -> [Cut039,Cut040,Cut041,Cut042,Cut038]
FEATURE [Part::Feature] Solid006  label="m4HeatSet"
  Placement = pos=(4.5,0,5.5) rot=(0,0,1;0rad)
  shape: bbox 6.396 x 4.801 x 6.396 mm, 237 faces (baked)
